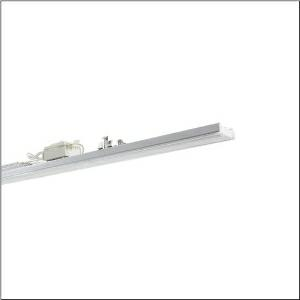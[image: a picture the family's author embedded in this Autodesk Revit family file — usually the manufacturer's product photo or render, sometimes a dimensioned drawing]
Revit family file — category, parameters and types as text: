
# Revit family: licross_r__21_recessed_mo_52tl11dn47xg_06fb
name_source: partatom
category: Lighting Fixtures
units: mm (PartAtom-declared; Revit-internal decimal feet)

## family parameters
Cut with Voids When Loaded = No
Host = Face
Light Source = No
Part Type = Normal
Room Calculation Point = No
Round Connector Dimension = Use Diameter
Shared = No

## types (1)
- --- (1 x LED, 7120 lm, 39.3 W, 4000K)
    Apparent Load = 39 VA
    CIE Flux Codes = 89 96 99 100 100
    Color Rendering = 80
    Color Temperature = 4000K
    Default Elevation = 1800 mm
    Description = Licross® 21 Recessed MO, luminaire insert, of sheet steel, galvanised, coil coated, white, length: 1.500mm, width: 66mm, height: 67mm, LED rated luminous flux: 7.120lm, light colour: 840, control gear: DALI 2, with plug, 5-pole, with phase selection, mains connection: 220..240V, AC, 50/60Hz, rated input power: 39W, internal wiring halogen-free, primary light control with lens, of plastic, primary optical cover: cover, of PMMA, light emission: direct distribution, primary light characteristic: symmetric, protection rating (complete): IP40, insulation class (complete): insulation class I (protective earthing), certification: CE, ENEC, VDE, UKCA, protection symbol: D if used in an environment without relevant dust loads with corresponding accessories, impact resistance: IK06, permissible ambient temperature for indoor applications: -25..+40°C, corresponds to IFS (International Featured Standards) requirements for safety and quality in the food industry, reducing of maximum allowable ambient temperature of 5°C with ceiling mounting, LABS conformity tested according to VDMA 24364:2018-05, packaging unit: 1 piece
    Height = 58 mm
    Lamp = 1 x LED
    Lamp Light Flux = 7120 lm
    Lamp Power = 39.3 W
    Lamp count = 1
    Length = 1500 mm
    Luminous efficacy = 181 lm/W
    Manufacturer = Siteco
    ModVariant = No
    Model = 52TL11DN47XG
    Mounting Place = Ceiling
    Mounting Type = Pendant
    Number of Poles = 1
    OnlyDefault = Yes
    Power Factor = 1
    Product Name = Licross® 21 Recessed MO
    Product group = luminaire insert | ceiling pendant
    ProductGroupID = 902
    Protection Class = Protection class I
    Protection Degree = IP 40
    RLX_Detail_Level = 1
    RLX_Emergency_Light_Flux = 0 lm
    RLX_Emergency_Type = 0
    RLX_Emergency_Type_DB = No
    RlxData = <blob elided: 24089 chars, md5=63b2d1e1>
    Socket = socket
    Standby Power = 0 W
    System Light Flux = 7120 lm
    System Power = 39 W
    Type Comments = factory setting: luminous flux: 100 % | dim-lin: 254 | 267 mA
    Type Image = l_1296930.jpg
    URL = http://relux.com
    VarID = @adj_148449
    Voltage = 0 V
    Weight = 0.00 kg
    Width = 66 mm

## geometry (parser evidence)
native form markers: Blend x4, Sweep x11
no freeform markers — native parametric forms only
